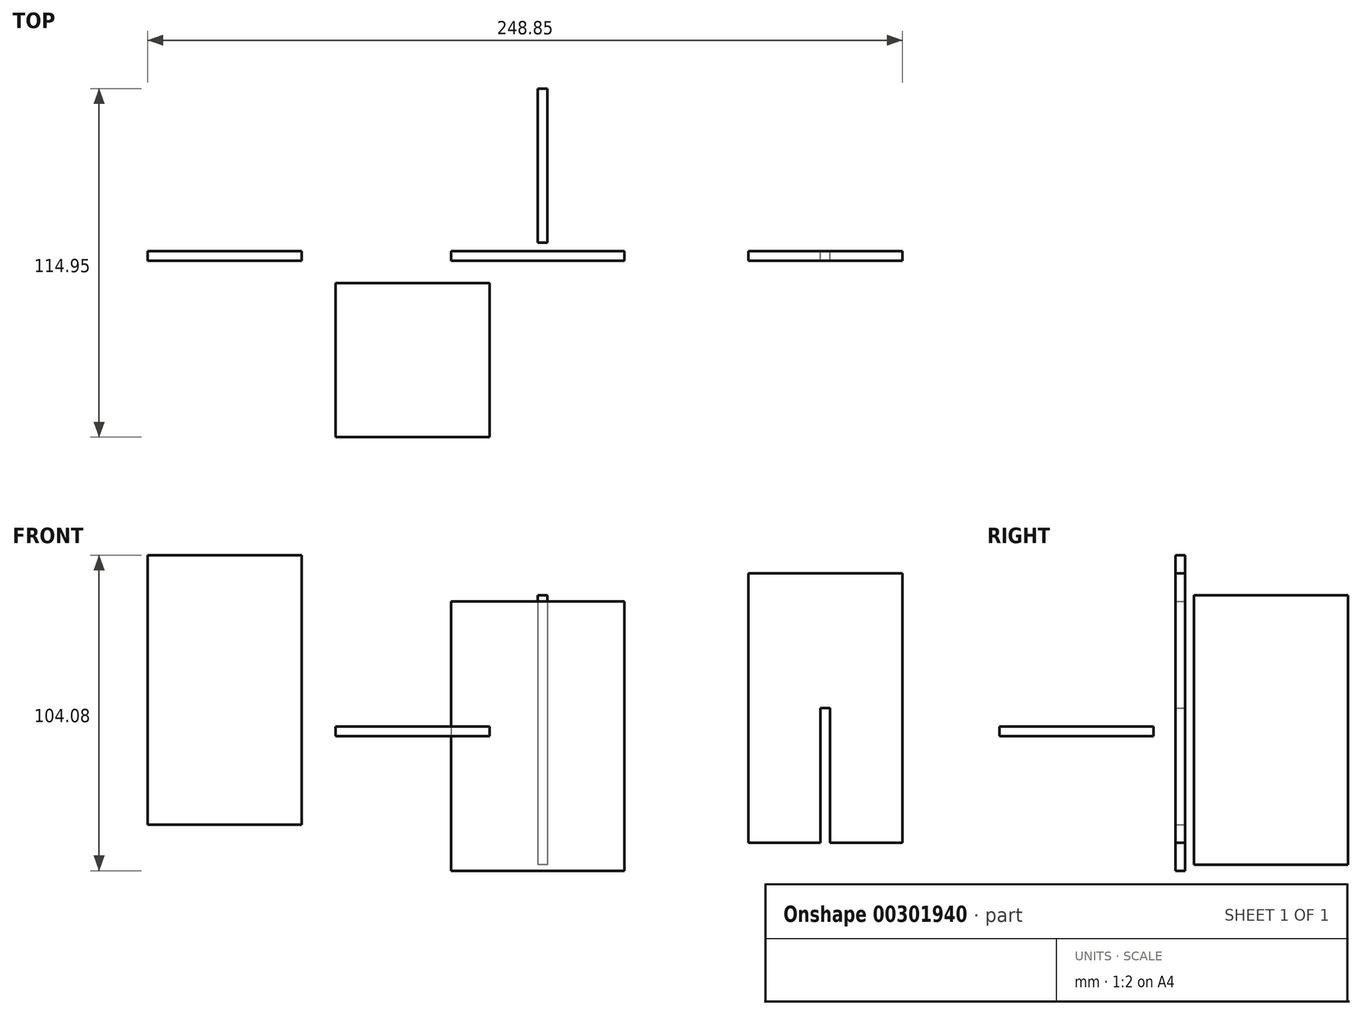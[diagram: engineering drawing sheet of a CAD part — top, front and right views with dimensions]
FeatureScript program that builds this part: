
annotation { "Feature Type Name" : "Feature", "Feature Type Description" : "" }
export const myFeature = defineFeature(function(context is Context, id is Id, definition is map)
    precondition{}
    {
        {
            var Q0;
            Q0=qCreatedBy(makeId("Front.planeOp"),FACE);
            var sketch = newSketch(context, id + "F0", { "sketchPlane" : qUnion([Q0])});
            skLineSegment(sketch, "E0.bottom", {"start": v(-28.57, 44.45) * mm, "end": v(28.58, 44.45) * mm});
            skLineSegment(sketch, "E0.top", {"start": v(-28.58, -44.45) * mm, "end": v(28.57, -44.45) * mm});
            skLineSegment(sketch, "E0.left", {"start": v(-28.57, 44.45) * mm, "end": v(-28.58, -44.45) * mm});
            skLineSegment(sketch, "E0.right", {"start": v(28.58, 44.45) * mm, "end": v(28.57, -44.45) * mm});
            skPoint(sketch, "E0.middle", {"position": v(0, 0) * mm});
            skSolve(sketch);
        }
        {
            var Q0;
            Q0=makeQuery(id+"F0.imprint","IMPRINT",FACE,{"disambiguationData":[TD([[makeQuery(id+"F0.imprint","IMPRINT",EDGE,{"derivedFrom":sQuery(id+"F0.wireOp",EDGE,"E0.bottom")}),-1.0]])]});
            extrude(context, id + "F1", {"entities" : qUnion([Q0]), "depth" : 3.17 * mm});
        }
        {
            var Q0;
            Q0=makeQuery(id+"F1.opExtrude","SWEPT_BODY",BODY,{"disambiguationData":[OSD([sQuery(id+"F0.wireOp",EDGE,"E0.bottom"),sQuery(id+"F0.wireOp",EDGE,"E0.top"),sQuery(id+"F0.wireOp",EDGE,"E0.left"),sQuery(id+"F0.wireOp",EDGE,"E0.right")])]});
            transform(context, id + "F2", {"entities" : qUnion([Q0]), "transformType" : TransformType.TRANSLATION_3D, "dx" : 0 * mm, "dy" : 0 * mm, "dz" : 0 * mm, "makeCopy" : true});
        }
        {
            var Q0;
            Q0=makeQuery(id+"F2.opPattern","COPY",BODY,{"derivedFrom":makeQuery(id+"F1.opExtrude","SWEPT_BODY",BODY,{"disambiguationData":[OSD([sQuery(id+"F0.wireOp",EDGE,"E0.bottom"),sQuery(id+"F0.wireOp",EDGE,"E0.top"),sQuery(id+"F0.wireOp",EDGE,"E0.left"),sQuery(id+"F0.wireOp",EDGE,"E0.right")])]}),"instanceName":"1"});
            deleteBodies(context, id + "F3", {"entities" : qUnion([Q0])});
        }
        {
            var Q0;
            Q0=qCreatedBy(makeId("Right.planeOp"),FACE);
            var sketch = newSketch(context, id + "F4", { "sketchPlane" : qUnion([Q0])});
            skLineSegment(sketch, "E1.bottom", {"start": v(2.87, 46.47) * mm, "end": v(53.67, 46.47) * mm});
            skLineSegment(sketch, "E1.top", {"start": v(2.87, -42.43) * mm, "end": v(53.67, -42.43) * mm});
            skLineSegment(sketch, "E1.left", {"start": v(2.87, 46.47) * mm, "end": v(2.87, -42.43) * mm});
            skLineSegment(sketch, "E1.right", {"start": v(53.67, 46.47) * mm, "end": v(53.67, -42.43) * mm});
            skSolve(sketch);
        }
        {
            var Q0;
            Q0=makeQuery(id+"F4.imprint","IMPRINT",FACE,{"disambiguationData":[TD([[makeQuery(id+"F4.imprint","IMPRINT",EDGE,{"derivedFrom":sQuery(id+"F4.wireOp",EDGE,"E1.bottom")}),-1.0]])]});
            extrude(context, id + "F5", {"entities" : qUnion([Q0]), "depth" : 3.17 * mm});
        }
        {
            var Q0;
            Q0=qCreatedBy(makeId("Top.planeOp"),FACE);
            var sketch = newSketch(context, id + "F6", { "sketchPlane" : qUnion([Q0])});
            skLineSegment(sketch, "E2.bottom", {"start": v(-66.6, -61.28) * mm, "end": v(-15.8, -61.28) * mm});
            skLineSegment(sketch, "E2.top", {"start": v(-66.6, -10.48) * mm, "end": v(-15.8, -10.48) * mm});
            skLineSegment(sketch, "E2.left", {"start": v(-66.6, -61.28) * mm, "end": v(-66.6, -10.48) * mm});
            skLineSegment(sketch, "E2.right", {"start": v(-15.8, -61.28) * mm, "end": v(-15.8, -10.48) * mm});
            skSolve(sketch);
        }
        {
            var Q0;
            Q0=makeQuery(id+"F6.imprint","IMPRINT",FACE,{"disambiguationData":[TD([[makeQuery(id+"F6.imprint","IMPRINT",EDGE,{"derivedFrom":sQuery(id+"F6.wireOp",EDGE,"E2.bottom")}),1.0]])]});
            extrude(context, id + "F7", {"entities" : qUnion([Q0]), "depth" : 3.17 * mm});
        }
        {
            var Q0;
            Q0=qCreatedBy(makeId("Front.planeOp"),FACE);
            var sketch = newSketch(context, id + "F8", { "sketchPlane" : qUnion([Q0])});
            skLineSegment(sketch, "E3.bottom", {"start": v(-128.57, 59.63) * mm, "end": v(-77.77, 59.63) * mm});
            skLineSegment(sketch, "E3.top", {"start": v(-128.57, -29.27) * mm, "end": v(-77.77, -29.27) * mm});
            skLineSegment(sketch, "E3.left", {"start": v(-128.57, 59.63) * mm, "end": v(-128.57, -29.27) * mm});
            skLineSegment(sketch, "E3.right", {"start": v(-77.77, 59.63) * mm, "end": v(-77.77, -29.27) * mm});
            skSolve(sketch);
        }
        {
            var Q0;
            Q0=makeQuery(id+"F8.imprint","IMPRINT",FACE,{"disambiguationData":[TD([[makeQuery(id+"F8.imprint","IMPRINT",EDGE,{"derivedFrom":sQuery(id+"F8.wireOp",EDGE,"E3.bottom")}),-1.0]])]});
            extrude(context, id + "F9", {"entities" : qUnion([Q0]), "depth" : 3.17 * mm});
        }
        {
            var Q0;
            Q0=qCreatedBy(makeId("Front.planeOp"),FACE);
            var sketch = newSketch(context, id + "F10", { "sketchPlane" : qUnion([Q0])});
            skLineSegment(sketch, "E4.bottom", {"start": v(69.48, 53.7) * mm, "end": v(120.28, 53.7) * mm});
            skLineSegment(sketch, "E4.left", {"start": v(69.48, 53.7) * mm, "end": v(69.48, -35.2) * mm});
            skLineSegment(sketch, "E4.right", {"start": v(120.28, 53.7) * mm, "end": v(120.28, -35.2) * mm});
            skLineSegment(sketch, "E5.top", {"start": v(96.47, 9.25) * mm, "end": v(93.3, 9.25) * mm});
            skLineSegment(sketch, "E5.left", {"start": v(96.47, -35.2) * mm, "end": v(96.47, 9.25) * mm});
            skLineSegment(sketch, "E5.right", {"start": v(93.3, -35.2) * mm, "end": v(93.3, 9.25) * mm});
            skLineSegment(sketch, "E6", {"start": v(120.28, -35.2) * mm, "end": v(96.47, -35.2) * mm});
            skLineSegment(sketch, "E7", {"start": v(93.3, -35.2) * mm, "end": v(69.48, -35.2) * mm});
            skSolve(sketch);
        }
        {
            var Q0;
            Q0=makeQuery(id+"F10.imprint","IMPRINT",FACE,{"disambiguationData":[TD([[makeQuery(id+"F10.imprint","IMPRINT",EDGE,{"derivedFrom":sQuery(id+"F10.wireOp",EDGE,"E4.bottom")}),-1.0]])]});
            extrude(context, id + "F11", {"entities" : qUnion([Q0]), "depth" : 3.17 * mm});
        }
    });
